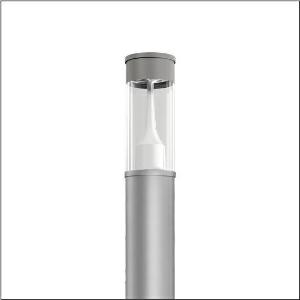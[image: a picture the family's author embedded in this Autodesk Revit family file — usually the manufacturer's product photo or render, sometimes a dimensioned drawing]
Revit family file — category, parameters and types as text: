
# Revit family: city-light_260_iq___pl1_2s_5xa5295cf14h_efd3
name_source: partatom
category: Lighting Fixtures
units: mm (PartAtom-declared; Revit-internal decimal feet)

## family parameters
Cut with Voids When Loaded = No
Host = Face
Light Source = No
Part Type = Normal
Room Calculation Point = No
Round Connector Dimension = Use Diameter
Shared = No

## types (1)
- --- (1 x LED, 2970 lm, 23.9 W, 2200K)
    Apparent Load = 24 VA
    CIE Flux Codes = 23 62 94 96 100
    Color Rendering = 70
    Color Temperature = 2200K
    Default Elevation = 1800 mm
    Description = City-Light 260 iQ, light pillar, Module 540 iQ-SR, primary light control with 3 zone facetted reflector, of plastic, silver coated, highly specular, structured, primary optical cover: cover, of PMMA, transparent, partly coated, light distribution: PL1.2s, primary light characteristic: symmetric, LED, High Power LED, rated luminous flux: 2.970lm, luminous efficacy: 124lm/W, light colour: 722, colour temperature: 2200K, control gear: ECG iQ, control: presetting dimming logarithmic, Street-Remote, Auto-Match, Temp-Guard, Lumen-Switch, Night-Set, Smart-Wire, Light-Fading, Desk-Remote (wireless, voltage-free reading and setting of iQ features in the workshop via application-optimized NFC function/RFID function), optimised constant luminous flux control (CLO 2.0), with terminal, 6-pole, max. 2.5mm², mains connection: 230..240V, AC, 50/60Hz, start of lifetime: 24W, end of service life: 26W, reduction: 12W, luminaire housing, cylindrical, of extruded aluminium section, coated, Siteco® metallic grey (DB 702S), length: 2.600mm, diameter: 200mm, Module 540 iQ-SR, traffic white (RAL 9016), equipment: standard, protection rating (complete): IP65, insulation class (complete): insulation class II (safety insulation), certification: CE, ENEC, VDE, packaging unit: 1 piece

Light Distribution: PL1.2s
    Height = 500 mm
    Lamp = 1 x LED
    Lamp Light Flux = 2970 lm
    Lamp Power = 23.9 W
    Lamp count = 1
    Length = 200 mm  [stored 0.656168 ft]
    Luminous efficacy = 124 lm/W
    Manufacturer = Siteco
    ModVariant = No
    Model = 5XA5295CF14H
    Mounting Place = Floor
    Mounting Type = Freestanding
    Number of Poles = 1
    OnlyDefault = Yes
    Power Factor = 1
    Product Name = City-Light 260 iQ | PL1.2s
    Product group = light pillar
    ProductGroupID = 1303
    Protection Class = Protection class II
    Protection Degree = IP 65
    RLX_Detail_Level = 1
    RLX_Emergency_Light_Flux = 0 lm
    RLX_Emergency_Type = 0
    RLX_Emergency_Type_DB = No
    RlxData = <blob elided: 28713 chars, md5=1219a892>
    Socket = socket
    Standby Power = 0 W
    System Light Flux = 2970 lm
    System Power = 24 W
    Type Comments = factory setting: luminous flux: 100 % | dim-lin: 254 | 499 mA
    Type Image = l_1006920.jpg
    URL = http://relux.com
    VarID = @adj_094651
    Voltage = 0 V
    Weight = 0.00 kg
    Width = 0 mm  [stored 0 ft]

note: [stored X ft] marks values corroborated as IEEE doubles in the binary element streams (Revit-internal decimal feet)

## geometry (parser evidence)
native form markers: Blend x4, Sweep x9
no freeform markers — native parametric forms only
